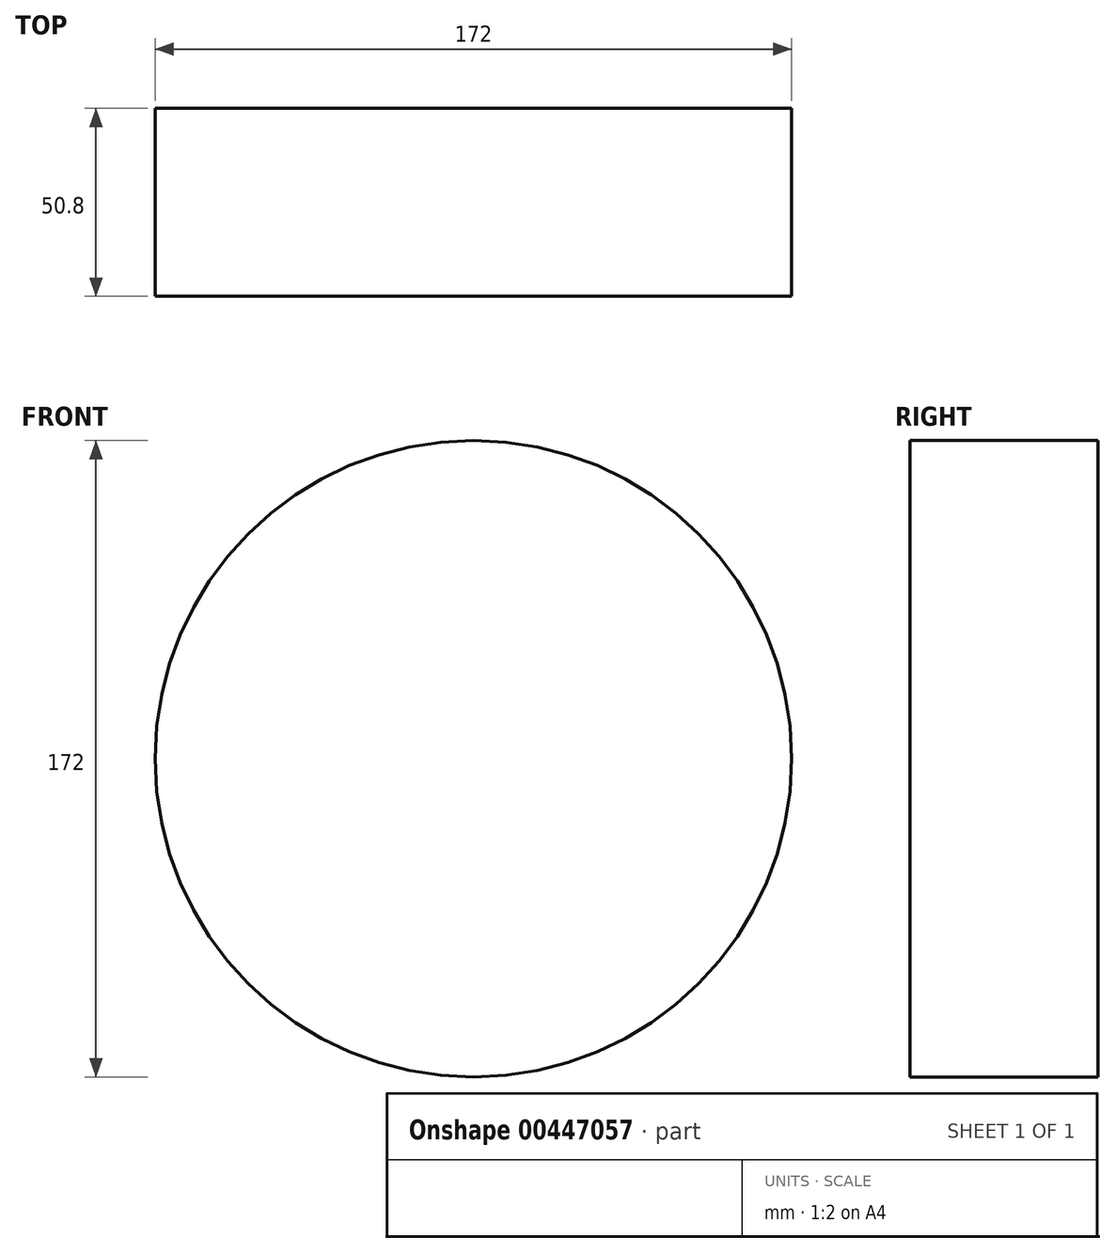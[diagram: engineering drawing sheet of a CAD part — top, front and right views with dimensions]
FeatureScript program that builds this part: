
annotation { "Feature Type Name" : "Feature", "Feature Type Description" : "" }
export const myFeature = defineFeature(function(context is Context, id is Id, definition is map)
    precondition{}
    {
        {
            var Q0;
            Q0=qCreatedBy(makeId("Front.planeOp"),FACE);
            var sketch = newSketch(context, id + "F0", { "sketchPlane" : qUnion([Q0])});
            skCircle(sketch, "E0", {"center": v(0, 0) * mm, "radius": 86 * mm});
            skSolve(sketch);
        }
        {
            var Q0;
            Q0=makeQuery(id+"F0.imprint","IMPRINT",FACE,{"disambiguationData":[TD([[makeQuery(id+"F0.imprint","IMPRINT",EDGE,{"derivedFrom":sQuery(id+"F0.wireOp",EDGE,"E0")}),1.0]])]});
            extrude(context, id + "F1", {"entities" : qUnion([Q0]), "depth" : 50.8 * mm});
        }
    });
